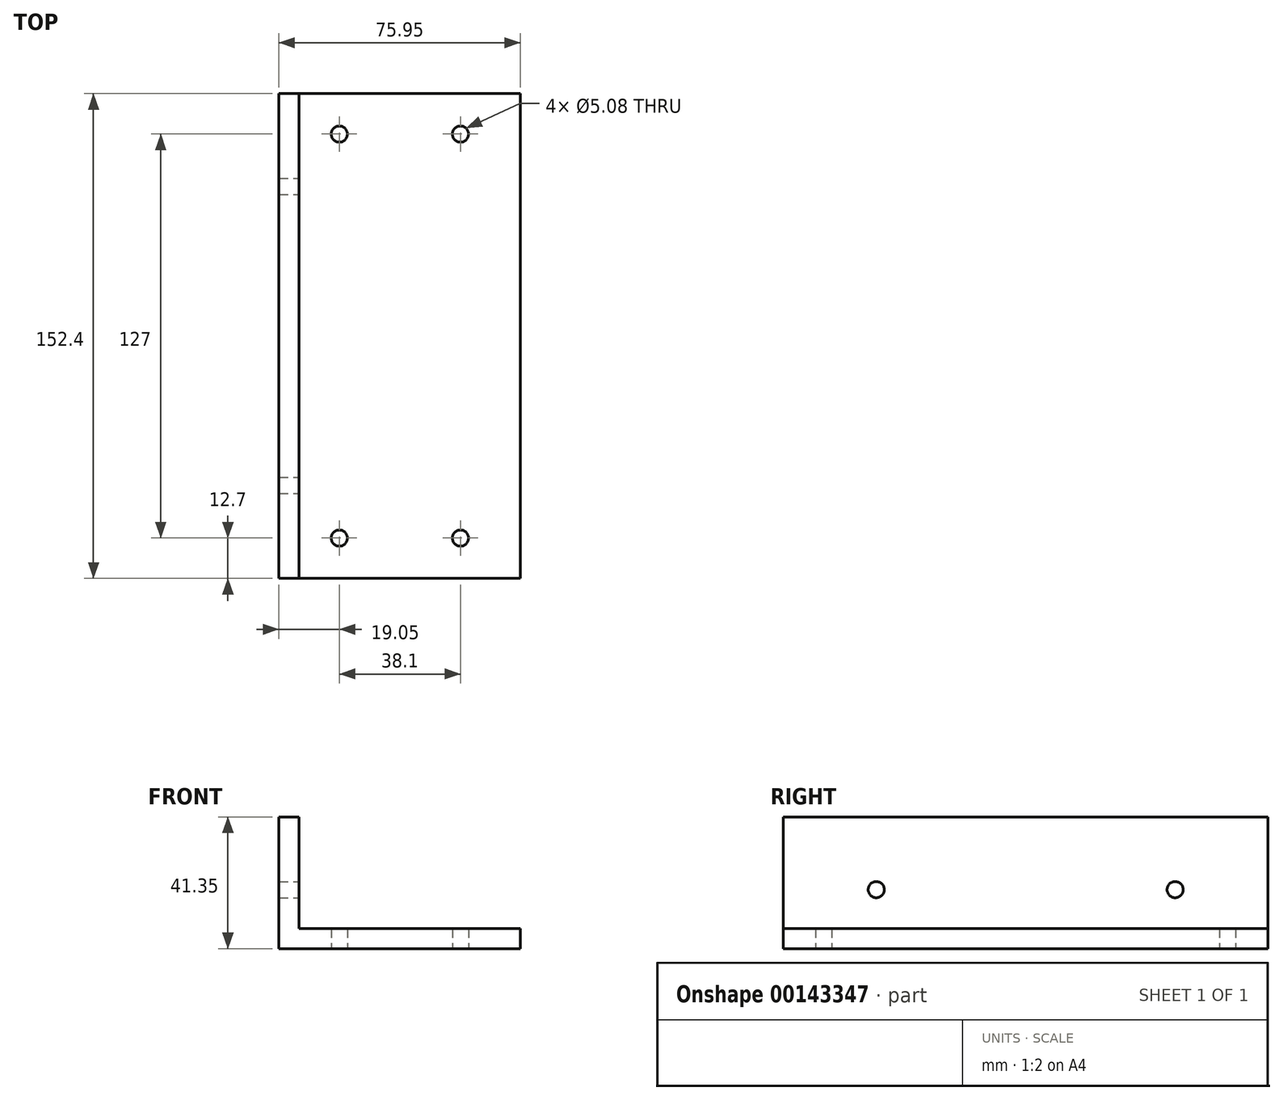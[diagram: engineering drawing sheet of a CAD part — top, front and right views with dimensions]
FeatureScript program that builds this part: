
annotation { "Feature Type Name" : "Feature", "Feature Type Description" : "" }
export const myFeature = defineFeature(function(context is Context, id is Id, definition is map)
    precondition{}
    {
        {
            var Q0;
            Q0=qCreatedBy(makeId("Top.planeOp"),FACE);
            var sketch = newSketch(context, id + "F0", { "sketchPlane" : qUnion([Q0])});
            skLineSegment(sketch, "E0.bottom", {"start": v(0, 0) * mm, "end": v(75.95, 0) * mm});
            skLineSegment(sketch, "E0.top", {"start": v(0, 152.4) * mm, "end": v(75.95, 152.4) * mm});
            skLineSegment(sketch, "E0.left", {"start": v(0, 0) * mm, "end": v(0, 152.4) * mm});
            skLineSegment(sketch, "E0.right", {"start": v(75.95, 0) * mm, "end": v(75.95, 152.4) * mm});
            skSolve(sketch);
        }
        {
            var Q0;
            Q0=makeQuery(id+"F0.imprint","IMPRINT",FACE,{"disambiguationData":[TD([[makeQuery(id+"F0.imprint","IMPRINT",EDGE,{"derivedFrom":sQuery(id+"F0.wireOp",EDGE,"E0.bottom")}),1.0]])]});
            var sketch = newSketch(context, id + "F1", { "sketchPlane" : qUnion([Q0])});
            skLineSegment(sketch, "E1.bottom", {"start": v(0, 0) * mm, "end": v(6.35, 0) * mm});
            skLineSegment(sketch, "E1.top", {"start": v(0, 152.4) * mm, "end": v(6.35, 152.4) * mm});
            skLineSegment(sketch, "E1.left", {"start": v(0, 0) * mm, "end": v(0, 152.4) * mm});
            skLineSegment(sketch, "E1.right", {"start": v(6.35, 0) * mm, "end": v(6.35, 152.4) * mm});
            skLineSegment(sketch, "E2", {"start": v(0, 0) * mm, "end": v(75.7, 0) * mm});
            skLineSegment(sketch, "E3.bottom", {"start": v(75.7, 0) * mm, "end": v(69.34, 0) * mm});
            skLineSegment(sketch, "E3.top", {"start": v(75.7, 152.4) * mm, "end": v(69.34, 152.4) * mm});
            skLineSegment(sketch, "E3.left", {"start": v(75.7, 0) * mm, "end": v(75.7, 152.4) * mm});
            skLineSegment(sketch, "E3.right", {"start": v(69.34, 0) * mm, "end": v(69.34, 152.4) * mm});
            skSolve(sketch);
        }
        {
            var Q0;
            Q0=makeQuery(id+"F0.imprint","IMPRINT",FACE,{"disambiguationData":[TD([[makeQuery(id+"F0.imprint","IMPRINT",EDGE,{"derivedFrom":sQuery(id+"F0.wireOp",EDGE,"E0.bottom")}),1.0]])]});
            extrude(context, id + "F2", {"entities" : qUnion([Q0]), "oppositeDirection" : true, "depth" : 6.35 * mm});
        }
        {
            var Q0;
            Q0=makeQuery(id+"F1.imprint","IMPRINT",FACE,{"disambiguationData":[TD([[makeQuery(id+"F1.imprint","IMPRINT",EDGE,{"derivedFrom":sQuery(id+"F1.wireOp",EDGE,"E1.top")}),-1.0]])]});
            var Q1;
            Q1=makeQuery(id+"F1.imprint","IMPRINT",FACE,{"disambiguationData":[TD([[makeQuery(id+"F1.imprint","IMPRINT",EDGE,{"derivedFrom":sQuery(id+"F1.wireOp",EDGE,"E3.bottom")}),1.0]])]});
            extrude(context, id + "F3", {"entities" : qUnion([Q0, Q1]), "operationType" : NewBodyOperationType.ADD, "depth" : 35 * mm});
        }
        {
            var Q0;
            Q0=makeQuery(id+"F2.opExtrude","CAP_FACE",FACE,{"disambiguationData":[OSD([sQuery(id+"F0.wireOp",EDGE,"E0.bottom"),sQuery(id+"F0.wireOp",EDGE,"E0.top"),sQuery(id+"F0.wireOp",EDGE,"E0.left"),sQuery(id+"F0.wireOp",EDGE,"E0.right")])],"isStart":false});
            var sketch = newSketch(context, id + "F4", { "sketchPlane" : qUnion([Q0])});
            skLineSegment(sketch, "E4", {"start": v(0, 0) * mm, "end": v(38.1, 0) * mm});
            skLineSegment(sketch, "E5", {"start": v(38.1, 0) * mm, "end": v(38.1, -76.2) * mm});
            skPoint(sketch, "E6.middle", {"position": v(38.1, -76.2) * mm});
            skCircle(sketch, "E7", {"center": v(57.15, -12.7) * mm, "radius": 2.54 * mm});
            skCircle(sketch, "E8", {"center": v(19.05, -12.7) * mm, "radius": 2.54 * mm});
            skCircle(sketch, "E9", {"center": v(19.05, -139.7) * mm, "radius": 2.54 * mm});
            skCircle(sketch, "E10", {"center": v(57.15, -139.7) * mm, "radius": 2.54 * mm});
            skSolve(sketch);
        }
        {
            var Q0;
            Q0 = qSketchRegion(id + "F4", true);
            extrude(context, id + "F5", {"entities" : qUnion([Q0]), "operationType" : NewBodyOperationType.REMOVE, "endBound" : BoundingType.THROUGH_ALL, "oppositeDirection" : true, "depth" : 25.4 * mm});
        }
        {
            var Q0;
            Q0=makeQuery(id+"F3.opExtrude","SWEPT_FACE",FACE,{"disambiguationData":[OSD([sQuery(id+"F1.wireOp",EDGE,"E1.right")])]});
            var sketch = newSketch(context, id + "F6", { "sketchPlane" : qUnion([Q0])});
            skLineSegment(sketch, "E11", {"start": v(0, 0) * mm, "end": v(76.2, 0) * mm});
            skLineSegment(sketch, "E12", {"start": v(76.2, 0) * mm, "end": v(29.21, 0) * mm});
            skLineSegment(sketch, "E13", {"start": v(29.21, 0) * mm, "end": v(29.21, 12.2) * mm});
            skLineSegment(sketch, "E14", {"start": v(29.21, 12.2) * mm, "end": v(123.2, 12.2) * mm});
            skLineSegment(sketch, "E15", {"start": v(123.2, 12.2) * mm, "end": v(123.2, 0) * mm});
            skCircle(sketch, "E16", {"center": v(29.21, 12.2) * mm, "radius": 2.54 * mm});
            skCircle(sketch, "E17", {"center": v(123.2, 12.2) * mm, "radius": 2.54 * mm});
            skSolve(sketch);
        }
        {
            var Q0;
            Q0 = qSketchRegion(id + "F6", true);
            extrude(context, id + "F7", {"entities" : qUnion([Q0]), "operationType" : NewBodyOperationType.REMOVE, "endBound" : BoundingType.THROUGH_ALL, "oppositeDirection" : true, "depth" : 25.4 * mm, "hasSecondDirection" : true, "secondDirectionBound" : SecondDirectionBoundingType.THROUGH_ALL, "secondDirectionOppositeDirection" : false, "secondDirectionDepth" : 25.4 * mm});
        }
    });
